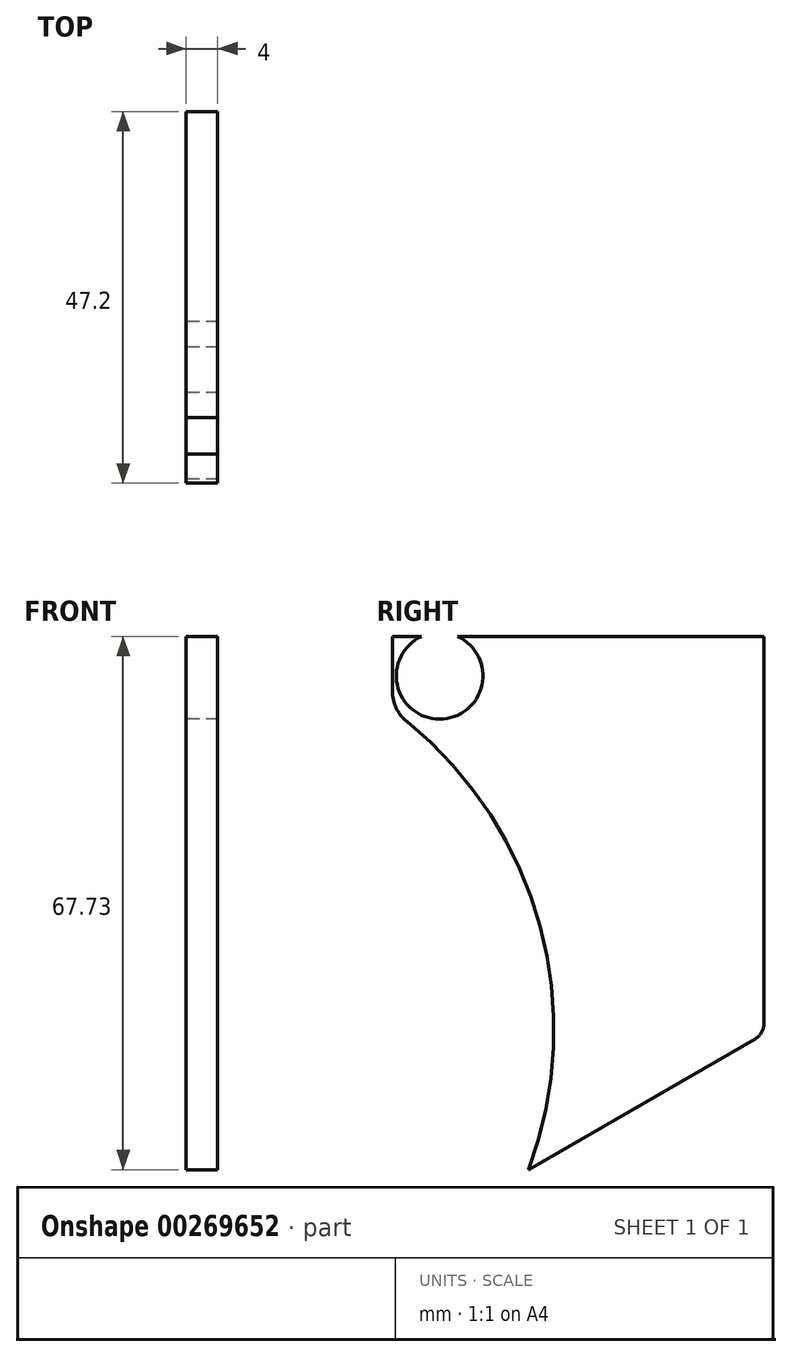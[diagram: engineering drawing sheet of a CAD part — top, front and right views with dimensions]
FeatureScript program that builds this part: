
annotation { "Feature Type Name" : "Feature", "Feature Type Description" : "" }
export const myFeature = defineFeature(function(context is Context, id is Id, definition is map)
    precondition{}
    {
        {
            var Q0;
            Q0=qCreatedBy(makeId("Right.planeOp"),FACE);
            var sketch = newSketch(context, id + "F0", { "sketchPlane" : qUnion([Q0])});
            skLineSegment(sketch, "E0", {"start": v(50, -52.08) * mm, "end": v(50, 0) * mm});
            skLineSegment(sketch, "E1", {"start": v(50, 0) * mm, "end": v(0, 0) * mm});
            skArc(sketch, "E2", {"start": v(-77.52, -32.91) * mm, "mid": v(-15.33, -98.32) * mm, "end": v(0, -9.38) * mm});
            skLineSegment(sketch, "E3", {"start": v(0, 0) * mm, "end": v(0, -9.38) * mm});
            skLineSegment(sketch, "E4", {"start": v(50, -52.08) * mm, "end": v(28.18, -64.68) * mm});
            skCircle(sketch, "E5", {"center": v(-30, -50) * mm, "radius": 50.5 * mm, "construction": true});
            skLineSegment(sketch, "E6", {"start": v(-77.52, -32.91) * mm, "end": v(-87.52, -32.91) * mm});
            skLineSegment(sketch, "E7", {"start": v(-15, -140.5) * mm, "end": v(-15, -108.1) * mm});
            skLineSegment(sketch, "E8", {"start": v(-45, -108.1) * mm, "end": v(-45, -140.5) * mm});
            skLineSegment(sketch, "E9", {"start": v(-45, -140.5) * mm, "end": v(-15, -140.5) * mm});
            skArc(sketch, "E10", {"start": v(-15, -108.1) * mm, "mid": v(12.54, -92.3) * mm, "end": v(28.18, -64.68) * mm});
            skArc(sketch, "E11.trimOffspring", {"start": v(-87.52, -32.91) * mm, "mid": v(-82.23, -79.54) * mm, "end": v(-45, -108.1) * mm});
            skLineSegment(sketch, "E12", {"start": v(-30, -50) * mm, "end": v(-30, -129.79) * mm, "construction": true});
            skSolve(sketch);
        }
        {
            var Q0;
            Q0=qSketchRegion(id+"F0",true);
            extrude(context, id + "F1", {"entities" : qUnion([Q0]), "depth" : 34 * mm});
        }
        {
            var Q0;
            Q0=makeQuery(id+"F1.opExtrude","SWEPT_EDGE",EDGE,{"disambiguationData":[OSD([sQuery(id+"F0.wireOp",EDGE,"E0"),sQuery(id+"F0.wireOp",EDGE,"E4")])]});
            var Q1;
            Q1=makeQuery(id+"F1.opExtrude","SWEPT_EDGE",EDGE,{"disambiguationData":[OSD([sQuery(id+"F0.wireOp",EDGE,"E2"),sQuery(id+"F0.wireOp",EDGE,"E3")])]});
            fillet(context, id + "F2", {"entities" : qUnion([Q0, Q1]), "radius" : 5 * mm, "tangentPropagation" : true, "allowEdgeOverflow" : false});
        }
        {
            var Q0;
            Q0=makeQuery(id+"F1.opExtrude","SWEPT_FACE",FACE,{"disambiguationData":[OSD([sQuery(id+"F0.wireOp",EDGE,"E1")])]});
            var Q1;
            Q1=makeQuery(id+"F1.opExtrude","SWEPT_FACE",FACE,{"disambiguationData":[OSD([sQuery(id+"F0.wireOp",EDGE,"E2")])]});
            var Q2;
            Q2=makeQuery(id+"F2.opFillet","BLEND_FACE",FACE,{"disambiguationData":[OSD([sQuery(id+"F0.wireOp",EDGE,"E2"),sQuery(id+"F0.wireOp",EDGE,"E3")])]});
            var Q3;
            Q3=makeQuery(id+"F1.opExtrude","SWEPT_FACE",FACE,{"disambiguationData":[OSD([sQuery(id+"F0.wireOp",EDGE,"E3")])]});
            var Q4;
            Q4=makeQuery(id+"F1.opExtrude","SWEPT_FACE",FACE,{"disambiguationData":[OSD([sQuery(id+"F0.wireOp",EDGE,"E6")])]});
            var Q5;
            Q5=makeQuery(id+"F1.opExtrude","SWEPT_FACE",FACE,{"disambiguationData":[OSD([sQuery(id+"F0.wireOp",EDGE,"E9")])]});
            shell(context, id + "F3", {"entities" : qUnion([Q0, Q1, Q2, Q3, Q4, Q5]), "thickness" : 2.4 * mm});
        }
        {
            var Q0;
            Q0=makeQuery(id+"F1.opExtrude","CAP_FACE",FACE,{"disambiguationData":[OSD([sQuery(id+"F0.wireOp",EDGE,"E0"),sQuery(id+"F0.wireOp",EDGE,"E1"),sQuery(id+"F0.wireOp",EDGE,"E2"),sQuery(id+"F0.wireOp",EDGE,"E3"),sQuery(id+"F0.wireOp",EDGE,"E4"),sQuery(id+"F0.wireOp",EDGE,"E6"),sQuery(id+"F0.wireOp",EDGE,"E7"),sQuery(id+"F0.wireOp",EDGE,"E8"),sQuery(id+"F0.wireOp",EDGE,"E9"),sQuery(id+"F0.wireOp",EDGE,"E10"),sQuery(id+"F0.wireOp",EDGE,"E11.trimOffspring")])],"isStart":false});
            var sketch = newSketch(context, id + "F4", { "sketchPlane" : qUnion([Q0])});
            skArc(sketch, "E13.0", {"start": v(-17.9, -99.03) * mm, "mid": v(3.32, -87.94) * mm, "end": v(17.06, -68.32) * mm, "construction": true});
            skArc(sketch, "E14", {"start": v(-17.9, -108.77) * mm, "mid": v(12.64, -92.2) * mm, "end": v(28.89, -61.5) * mm});
            skPoint(sketch, "E15.orphan", {"position": v(1.85, -10.8) * mm});
            skArc(sketch, "E16", {"start": v(-77.52, -32.91) * mm, "mid": v(-47.7, -97.3) * mm, "end": v(17.06, -68.32) * mm});
            skLineSegment(sketch, "E17.0", {"start": v(28.89, -61.5) * mm, "end": v(17.06, -68.32) * mm});
            skPoint(sketch, "E18.orphan", {"position": v(26.09, -63.11) * mm});
            skPoint(sketch, "E19.orphan", {"position": v(-17.4, -106.2) * mm});
            skPoint(sketch, "E20.orphan", {"position": v(46.3, -51.44) * mm});
            skPoint(sketch, "E21.orphan", {"position": v(28.18, -64.68) * mm});
            skPoint(sketch, "E22.orphan", {"position": v(-15, -108.1) * mm});
            skLineSegment(sketch, "E23", {"start": v(-17.9, -99.03) * mm, "end": v(-17.9, -108.77) * mm});
            skSolve(sketch);
        }
        {
            var Q0;
            Q0=qSketchRegion(id+"F4",true);
            var Q1;
            {var subQ0=sQuery(id+"F0.wireOp",EDGE,"E11.trimOffspring");var subQ1=sQuery(id+"F0.wireOp",EDGE,"E10");var subQ2=sQuery(id+"F0.wireOp",EDGE,"E9");var subQ3=sQuery(id+"F0.wireOp",EDGE,"E8");var subQ4=sQuery(id+"F0.wireOp",EDGE,"E7");var subQ5=sQuery(id+"F0.wireOp",EDGE,"E6");var subQ6=sQuery(id+"F0.wireOp",EDGE,"E4");var subQ7=sQuery(id+"F0.wireOp",EDGE,"E3");var subQ8=sQuery(id+"F0.wireOp",EDGE,"E2");var subQ9=sQuery(id+"F0.wireOp",EDGE,"E1");var subQ10=sQuery(id+"F0.wireOp",EDGE,"E0");Q1=makeQuery(id+"F3.opShell","OFFSET_FACE",FACE,{"disambiguationData":[OSD([subQ10,subQ9,subQ8,subQ7,subQ6,subQ5,subQ4,subQ3,subQ2,subQ1,subQ0]),TDD([makeQuery(id+"F1.opExtrude","CAP_FACE",FACE,{"disambiguationData":[OSD([subQ10,subQ9,subQ8,subQ7,subQ6,subQ5,subQ4,subQ3,subQ2,subQ1,subQ0])],"isStart":true})])]});}
            extrude(context, id + "F5", {"entities" : qUnion([Q0]), "operationType" : NewBodyOperationType.ADD, "endBound" : BoundingType.UP_TO_SURFACE, "oppositeDirection" : true, "endBoundEntityFace" : qUnion([Q1]), "depth" : 25 * mm});
        }
        {
            var Q0;
            Q0=makeQuery(id+"F1.opExtrude","CAP_FACE",FACE,{"disambiguationData":[OSD([sQuery(id+"F0.wireOp",EDGE,"E0"),sQuery(id+"F0.wireOp",EDGE,"E1"),sQuery(id+"F0.wireOp",EDGE,"E2"),sQuery(id+"F0.wireOp",EDGE,"E3"),sQuery(id+"F0.wireOp",EDGE,"E4")])],"isStart":true});
            var sketch = newSketch(context, id + "F6", { "sketchPlane" : qUnion([Q0])});
            skCircle(sketch, "E24", {"center": v(-6, -5) * mm, "radius": 2.5 * mm});
            skCircle(sketch, "E25", {"center": v(-15.77, -82.6) * mm, "radius": 2.5 * mm});
            skArc(sketch, "E26.0", {"start": v(77.52, -32.91) * mm, "mid": v(16.45, -98.65) * mm, "end": v(-1.85, -10.8) * mm, "construction": true});
            skLineSegment(sketch, "E27", {"start": v(30, -50) * mm, "end": v(-6, -5) * mm, "construction": true});
            skLineSegment(sketch, "E28", {"start": v(30, -50) * mm, "end": v(-15.77, -82.6) * mm, "construction": true});
            skLineSegment(sketch, "E29", {"start": v(-6, -5) * mm, "end": v(-15.77, -82.6) * mm, "construction": true});
            skSolve(sketch);
        }
        {
            var Q0;
            Q0=qSketchRegion(id+"F6",true);
            var Q1;
            Q1=makeQuery(id+"F1.opExtrude","CAP_FACE",FACE,{"disambiguationData":[OSD([sQuery(id+"F0.wireOp",EDGE,"E0"),sQuery(id+"F0.wireOp",EDGE,"E1"),sQuery(id+"F0.wireOp",EDGE,"E2"),sQuery(id+"F0.wireOp",EDGE,"E3"),sQuery(id+"F0.wireOp",EDGE,"E4"),sQuery(id+"F0.wireOp",EDGE,"E6"),sQuery(id+"F0.wireOp",EDGE,"E7"),sQuery(id+"F0.wireOp",EDGE,"E8"),sQuery(id+"F0.wireOp",EDGE,"E9"),sQuery(id+"F0.wireOp",EDGE,"E10"),sQuery(id+"F0.wireOp",EDGE,"E11.trimOffspring")])],"isStart":true});
            extrude(context, id + "F7", {"entities" : qUnion([Q0]), "operationType" : NewBodyOperationType.REMOVE, "endBound" : BoundingType.THROUGH_ALL, "oppositeDirection" : true, "endBoundEntityFace" : qUnion([Q1]), "depth" : 25 * mm});
        }
        {
            var Q0;
            Q0=makeQuery(id+"F5.opExtrude","SWEPT_EDGE",EDGE,{"disambiguationData":[OSD([sQuery(id+"F4.wireOp",EDGE,"E16"),sQuery(id+"F4.wireOp",EDGE,"E23")])]});
            fillet(context, id + "F8", {"entities" : qUnion([Q0]), "radius" : 5 * mm, "tangentPropagation" : true, "allowEdgeOverflow" : false});
        }
        {
            var Q0;
            Q0=makeQuery(id+"F1.opExtrude","SWEPT_FACE",FACE,{"disambiguationData":[OSD([sQuery(id+"F0.wireOp",EDGE,"E10")])]});
            shell(context, id + "F9", {"entities" : qUnion([Q0]), "thickness" : 2.4 * mm});
        }
        {
            var Q0;
            {var subQ0=sQuery(id+"F0.wireOp",EDGE,"E4");var subQ1=sQuery(id+"F0.wireOp",EDGE,"E0");var subQ2=sQuery(id+"F0.wireOp",EDGE,"E3");var subQ3=sQuery(id+"F0.wireOp",EDGE,"E2");var subQ4=sQuery(id+"F0.wireOp",EDGE,"E1");var subQ5=sQuery(id+"F0.wireOp",EDGE,"E11.trimOffspring");var subQ6=sQuery(id+"F0.wireOp",EDGE,"E10");var subQ7=sQuery(id+"F0.wireOp",EDGE,"E9");var subQ8=sQuery(id+"F0.wireOp",EDGE,"E8");var subQ9=sQuery(id+"F0.wireOp",EDGE,"E7");var subQ10=sQuery(id+"F0.wireOp",EDGE,"E6");Q0=makeQuery(id+"F5.boolean.opBoolean","SPLIT",FACE,{"disambiguationData":[TD([makeQuery(id+"F1.opExtrude","SWEPT_FACE",FACE,{"disambiguationData":[OSD([subQ4])]})])],"derivedFrom":makeQuery(id+"F3.opShell","OFFSET_FACE",FACE,{"disambiguationData":[OSD([subQ1,subQ4,subQ3,subQ2,subQ0,subQ10,subQ9,subQ8,subQ7,subQ6,subQ5]),TDD([makeQuery(id+"F1.opExtrude","CAP_FACE",FACE,{"disambiguationData":[OSD([subQ1,subQ4,subQ3,subQ2,subQ0,subQ10,subQ9,subQ8,subQ7,subQ6,subQ5])],"isStart":true})])]})});}
            cPlane(context, id + "F10", {"entities" : qUnion([Q0]), "cplaneType" : CPlaneType.OFFSET, "offset" : 7 * mm, "width" : 150 * mm, "height" : 150 * mm});
        }
        {
            var Q0;
            Q0=qCreatedBy(id+"F10.planeOp",FACE);
            var sketch = newSketch(context, id + "F11", { "sketchPlane" : qUnion([Q0])});
            skLineSegment(sketch, "E30.0", {"start": v(47.6, 0) * mm, "end": v(0, 0) * mm});
            skLineSegment(sketch, "E31.0", {"start": v(47.6, -49.19) * mm, "end": v(47.6, 0) * mm});
            skArc(sketch, "E32.0", {"start": v(47.6, -49.19) * mm, "mid": v(47.25, -50.49) * mm, "end": v(46.3, -51.44) * mm});
            skLineSegment(sketch, "E33.0", {"start": v(46.3, -51.44) * mm, "end": v(17.06, -68.32) * mm});
            skArc(sketch, "E34.0", {"start": v(17.06, -68.32) * mm, "mid": v(18.82, -37.09) * mm, "end": v(1.85, -10.8) * mm});
            skArc(sketch, "E35.0", {"start": v(1.85, -10.8) * mm, "mid": v(0.49, -9.08) * mm, "end": v(0, -6.93) * mm});
            skLineSegment(sketch, "E36.0", {"start": v(0, 0) * mm, "end": v(0, -6.93) * mm});
            skCircle(sketch, "E37.0", {"center": v(6, -5) * mm, "radius": 2.5 * mm});
            skSolve(sketch);
        }
        {
            var Q0;
            Q0=qSketchRegion(id+"F11",true);
            extrude(context, id + "F12", {"entities" : qUnion([Q0]), "operationType" : NewBodyOperationType.ADD, "depth" : 4 * mm});
        }
        {
            var Q0;
            Q0=makeQuery(id+"F6.imprint","IMPRINT",FACE,{"disambiguationData":[TD([[makeQuery(id+"F6.imprint","IMPRINT",EDGE,{"derivedFrom":sQuery(id+"F6.wireOp",EDGE,"E24")}),-1.0]])]});
            var sketch = newSketch(context, id + "F13", { "sketchPlane" : qUnion([Q0])});
            skCircle(sketch, "E38.0", {"center": v(-6, -5) * mm, "radius": 2.5 * mm});
            skCircle(sketch, "E39", {"center": v(-6, -5) * mm, "radius": 5 * mm});
            skSolve(sketch);
        }
        {
            var Q0;
            Q0=qSketchRegion(id+"F13",true);
            var Q1;
            {var subQ0=sQuery(id+"F0.wireOp",EDGE,"E4");var subQ1=sQuery(id+"F0.wireOp",EDGE,"E0");var subQ2=sQuery(id+"F0.wireOp",EDGE,"E3");var subQ3=sQuery(id+"F0.wireOp",EDGE,"E2");var subQ4=sQuery(id+"F0.wireOp",EDGE,"E1");var subQ5=sQuery(id+"F0.wireOp",EDGE,"E11.trimOffspring");var subQ6=sQuery(id+"F0.wireOp",EDGE,"E10");var subQ7=sQuery(id+"F0.wireOp",EDGE,"E9");var subQ8=sQuery(id+"F0.wireOp",EDGE,"E8");var subQ9=sQuery(id+"F0.wireOp",EDGE,"E7");var subQ10=sQuery(id+"F0.wireOp",EDGE,"E6");Q1=makeQuery(id+"F5.boolean.opBoolean","SPLIT",FACE,{"disambiguationData":[TD([makeQuery(id+"F1.opExtrude","SWEPT_FACE",FACE,{"disambiguationData":[OSD([subQ4])]})])],"derivedFrom":makeQuery(id+"F3.opShell","OFFSET_FACE",FACE,{"disambiguationData":[OSD([subQ1,subQ4,subQ3,subQ2,subQ0,subQ10,subQ9,subQ8,subQ7,subQ6,subQ5]),TDD([makeQuery(id+"F1.opExtrude","CAP_FACE",FACE,{"disambiguationData":[OSD([subQ1,subQ4,subQ3,subQ2,subQ0,subQ10,subQ9,subQ8,subQ7,subQ6,subQ5])],"isStart":false})])]})});}
            extrude(context, id + "F14", {"entities" : qUnion([Q0]), "operationType" : NewBodyOperationType.ADD, "endBound" : BoundingType.UP_TO_SURFACE, "oppositeDirection" : true, "endBoundEntityFace" : qUnion([Q1]), "depth" : 25 * mm});
        }
        {
            var Q0;
            Q0=makeQuery(id+"F6.imprint","IMPRINT",FACE,{"disambiguationData":[TD([[makeQuery(id+"F6.imprint","IMPRINT",EDGE,{"derivedFrom":sQuery(id+"F6.wireOp",EDGE,"E24")}),-1.0]])]});
            var sketch = newSketch(context, id + "F15", { "sketchPlane" : qUnion([Q0])});
            skLineSegment(sketch, "E40.0", {"start": v(45, -109.49) * mm, "end": v(45, -114.49) * mm});
            skLineSegment(sketch, "E41.0", {"start": v(15, -114.49) * mm, "end": v(15, -109.49) * mm});
            skLineSegment(sketch, "E42.bottom", {"start": v(5, -109.49) * mm, "end": v(15, -109.49) * mm});
            skLineSegment(sketch, "E42.top", {"start": v(5, -114.49) * mm, "end": v(15, -114.49) * mm});
            skLineSegment(sketch, "E42.left", {"start": v(5, -109.49) * mm, "end": v(5, -114.49) * mm});
            skLineSegment(sketch, "E42.right", {"start": v(55, -109.49) * mm, "end": v(55, -114.49) * mm});
            skLineSegment(sketch, "E43.trimOffspring", {"start": v(45, -109.49) * mm, "end": v(55, -109.49) * mm});
            skLineSegment(sketch, "E44.trimOffspring", {"start": v(45, -114.49) * mm, "end": v(55, -114.49) * mm});
            skPoint(sketch, "E45.orphan", {"position": v(15, -140.5) * mm});
            skPoint(sketch, "E46.orphan", {"position": v(45, -140.5) * mm});
            skPoint(sketch, "E47.orphan", {"position": v(45, -108.1) * mm});
            skPoint(sketch, "E48.orphan", {"position": v(15, -108.1) * mm});
            skSolve(sketch);
        }
        {
            var Q0;
            Q0=qSketchRegion(id+"F15",true);
            var Q1;
            Q1=makeQuery(id+"F1.opExtrude","CAP_FACE",FACE,{"disambiguationData":[OSD([sQuery(id+"F0.wireOp",EDGE,"E0"),sQuery(id+"F0.wireOp",EDGE,"E1"),sQuery(id+"F0.wireOp",EDGE,"E2"),sQuery(id+"F0.wireOp",EDGE,"E3"),sQuery(id+"F0.wireOp",EDGE,"E4"),sQuery(id+"F0.wireOp",EDGE,"E6"),sQuery(id+"F0.wireOp",EDGE,"E7"),sQuery(id+"F0.wireOp",EDGE,"E8"),sQuery(id+"F0.wireOp",EDGE,"E9"),sQuery(id+"F0.wireOp",EDGE,"E10"),sQuery(id+"F0.wireOp",EDGE,"E11.trimOffspring")])],"isStart":false});
            extrude(context, id + "F16", {"entities" : qUnion([Q0]), "operationType" : NewBodyOperationType.ADD, "endBound" : BoundingType.UP_TO_SURFACE, "oppositeDirection" : true, "endBoundEntityFace" : qUnion([Q1]), "depth" : 25 * mm});
        }
        {
            var Q0;
            {var subQ2=sQuery(id+"F0.wireOp",EDGE,"E9");var subQ5=sQuery(id+"F0.wireOp",EDGE,"E8");Q0=makeQuery(id+"F16.boolean.opBoolean","SPLIT",FACE,{"disambiguationData":[TD([makeQuery(id+"F1.opExtrude","SWEPT_FACE",FACE,{"disambiguationData":[OSD([subQ2])]})])],"derivedFrom":makeQuery(id+"F1.opExtrude","SWEPT_FACE",FACE,{"disambiguationData":[OSD([subQ5])]})});}
            var sketch = newSketch(context, id + "F17", { "sketchPlane" : qUnion([Q0])});
            skLineSegment(sketch, "E49", {"start": v(0, -127.5) * mm, "end": v(34, -127.5) * mm, "construction": true});
            skLineSegment(sketch, "E50", {"start": v(17, -140.5) * mm, "end": v(17, -114.49) * mm, "construction": true});
            skCircle(sketch, "E51", {"center": v(17, -127.5) * mm, "radius": 2.1 * mm});
            skSolve(sketch);
        }
        {
            var Q0;
            Q0=qSketchRegion(id+"F17",true);
            extrude(context, id + "F18", {"entities" : qUnion([Q0]), "operationType" : NewBodyOperationType.REMOVE, "endBound" : BoundingType.THROUGH_ALL, "oppositeDirection" : true, "depth" : 25 * mm});
        }
        {
            var Q0;
            Q0=makeQuery(id+"F12.opExtrude","CAP_FACE",FACE,{"disambiguationData":[OSD([sQuery(id+"F11.wireOp",EDGE,"E30.0"),sQuery(id+"F11.wireOp",EDGE,"E31.0"),sQuery(id+"F11.wireOp",EDGE,"E32.0"),sQuery(id+"F11.wireOp",EDGE,"E33.0"),sQuery(id+"F11.wireOp",EDGE,"E34.0"),sQuery(id+"F11.wireOp",EDGE,"E35.0"),sQuery(id+"F11.wireOp",EDGE,"E36.0"),sQuery(id+"F11.wireOp",EDGE,"E37.0")])],"isStart":true});
            var sketch = newSketch(context, id + "F19", { "sketchPlane" : qUnion([Q0])});
            skLineSegment(sketch, "E52.bottom", {"start": v(-63.7, 10.52) * mm, "end": v(126.2, 10.52) * mm});
            skLineSegment(sketch, "E52.top", {"start": v(-63.7, -153.85) * mm, "end": v(126.2, -153.85) * mm});
            skLineSegment(sketch, "E52.left", {"start": v(-63.7, 10.52) * mm, "end": v(-63.7, -153.85) * mm});
            skLineSegment(sketch, "E52.right", {"start": v(126.2, 10.52) * mm, "end": v(126.2, -153.85) * mm});
            skSolve(sketch);
        }
        {
            var Q0;
            {var subQ3=sQuery(id+"F11.wireOp",EDGE,"E34.0");Q0=makeQuery(id+"F19.imprint","IMPRINT",FACE,{"disambiguationData":[TD([[makeQuery(id+"F19.imprint","IMPRINT",EDGE,{"derivedFrom":makeQuery(id+"F12.opExtrude","CAP_EDGE",EDGE,{"disambiguationData":[OSD([subQ3])],"isStart":true})}),1.0]])]});}
            var sketch = newSketch(context, id + "F20", { "sketchPlane" : qUnion([Q0])});
            skCircle(sketch, "E53.0", {"center": v(-6, -5) * mm, "radius": 5.5 * mm});
            skSolve(sketch);
        }
        {
            var Q0;
            Q0 = qSketchRegion(id + "F19", true);
            extrude(context, id + "F21", {"entities" : qUnion([Q0]), "operationType" : NewBodyOperationType.REMOVE, "endBound" : BoundingType.THROUGH_ALL, "depth" : 25 * mm});
        }
        {
            var Q0;
            Q0=makeQuery(id+"F21.boolean.opBoolean","MERGE",FACE,{"derivedFrom":[makeQuery(id+"F12.opExtrude","CAP_FACE",FACE,{"disambiguationData":[OSD([sQuery(id+"F11.wireOp",EDGE,"E30.0"),sQuery(id+"F11.wireOp",EDGE,"E31.0"),sQuery(id+"F11.wireOp",EDGE,"E32.0"),sQuery(id+"F11.wireOp",EDGE,"E33.0"),sQuery(id+"F11.wireOp",EDGE,"E34.0"),sQuery(id+"F11.wireOp",EDGE,"E35.0"),sQuery(id+"F11.wireOp",EDGE,"E36.0"),sQuery(id+"F11.wireOp",EDGE,"E37.0")])],"isStart":true}),makeQuery(id+"F21.opExtrude","CAP_FACE",FACE,{"disambiguationData":[OSD([sQuery(id+"F19.wireOp",EDGE,"E52.bottom"),sQuery(id+"F19.wireOp",EDGE,"E52.top"),sQuery(id+"F19.wireOp",EDGE,"E52.left"),sQuery(id+"F19.wireOp",EDGE,"E52.right")])],"isStart":true})]});
            var sketch = newSketch(context, id + "F22", { "sketchPlane" : qUnion([Q0])});
            skLineSegment(sketch, "E54.0", {"start": v(-46.3, -51.44) * mm, "end": v(-17.06, -68.32) * mm});
            skLineSegment(sketch, "E55", {"start": v(-17.06, -68.32) * mm, "end": v(97.63, -13.25) * mm});
            skLineSegment(sketch, "E56", {"start": v(97.63, -13.25) * mm, "end": v(124.38, -131.2) * mm});
            skLineSegment(sketch, "E57", {"start": v(124.38, -131.2) * mm, "end": v(20.78, -157.05) * mm});
            skLineSegment(sketch, "E58", {"start": v(20.78, -157.05) * mm, "end": v(-89.3, -69.99) * mm});
            skLineSegment(sketch, "E59.0", {"start": v(-47.6, -49.19) * mm, "end": v(-47.6, 0) * mm});
            skArc(sketch, "E60", {"start": v(-47.6, -49.19) * mm, "mid": v(-47.25, -50.49) * mm, "end": v(-46.3, -51.44) * mm});
            skLineSegment(sketch, "E61", {"start": v(-64.25, 0) * mm, "end": v(-47.6, 0) * mm});
            skLineSegment(sketch, "E62", {"start": v(-64.25, 0) * mm, "end": v(-89.3, -69.99) * mm});
            skSolve(sketch);
        }
        {
            var Q0;
            Q0 = qSketchRegion(id + "F22", true);
            extrude(context, id + "F23", {"entities" : qUnion([Q0]), "operationType" : NewBodyOperationType.REMOVE, "oppositeDirection" : true, "depth" : 25 * mm});
        }
        {
            var Q0;
            Q0=makeQuery(id+"F12.opExtrude","CAP_FACE",FACE,{"disambiguationData":[OSD([sQuery(id+"F11.wireOp",EDGE,"E30.0"),sQuery(id+"F11.wireOp",EDGE,"E31.0"),sQuery(id+"F11.wireOp",EDGE,"E32.0"),sQuery(id+"F11.wireOp",EDGE,"E33.0"),sQuery(id+"F11.wireOp",EDGE,"E34.0"),sQuery(id+"F11.wireOp",EDGE,"E35.0"),sQuery(id+"F11.wireOp",EDGE,"E36.0"),sQuery(id+"F11.wireOp",EDGE,"E37.0")])],"isStart":false});
            var sketch = newSketch(context, id + "F24", { "sketchPlane" : qUnion([Q0])});
            skLineSegment(sketch, "E63.bottom", {"start": v(-62.95, 12.76) * mm, "end": v(97.94, 12.76) * mm});
            skLineSegment(sketch, "E63.top", {"start": v(-62.95, -97.2) * mm, "end": v(97.94, -97.2) * mm});
            skLineSegment(sketch, "E63.left", {"start": v(-62.95, 12.76) * mm, "end": v(-62.95, -97.2) * mm});
            skLineSegment(sketch, "E63.right", {"start": v(97.94, 12.76) * mm, "end": v(97.94, -97.2) * mm});
            skSolve(sketch);
        }
        {
            var Q0;
            Q0 = qSketchRegion(id + "F24", true);
            extrude(context, id + "F25", {"entities" : qUnion([Q0]), "operationType" : NewBodyOperationType.REMOVE, "endBound" : BoundingType.THROUGH_ALL, "depth" : 25 * mm});
        }
        {
            var Q0;
            Q0 = qSketchRegion(id + "F20", true);
            var Q1;
            Q1 = qConstructionFilter(qBodyType(qCreatedBy(id + "F20" ,EDGE), BodyType.WIRE), ConstructionObject.NO);
            extrude(context, id + "F26", {"entities" : qUnion([Q0]), "operationType" : NewBodyOperationType.REMOVE, "surfaceEntities" : qUnion([Q1]), "endBound" : BoundingType.THROUGH_ALL, "oppositeDirection" : true, "depth" : 25 * mm});
        }
        {
            var Q0;
            Q0=makeQuery(id+"F21.boolean.opBoolean","MERGE",FACE,{"derivedFrom":[makeQuery(id+"F12.opExtrude","CAP_FACE",FACE,{"disambiguationData":[OSD([sQuery(id+"F11.wireOp",EDGE,"E30.0"),sQuery(id+"F11.wireOp",EDGE,"E31.0"),sQuery(id+"F11.wireOp",EDGE,"E32.0"),sQuery(id+"F11.wireOp",EDGE,"E33.0"),sQuery(id+"F11.wireOp",EDGE,"E34.0"),sQuery(id+"F11.wireOp",EDGE,"E35.0"),sQuery(id+"F11.wireOp",EDGE,"E36.0"),sQuery(id+"F11.wireOp",EDGE,"E37.0")])],"isStart":true}),makeQuery(id+"F21.opExtrude","CAP_FACE",FACE,{"disambiguationData":[OSD([sQuery(id+"F19.wireOp",EDGE,"E52.bottom"),sQuery(id+"F19.wireOp",EDGE,"E52.top"),sQuery(id+"F19.wireOp",EDGE,"E52.left"),sQuery(id+"F19.wireOp",EDGE,"E52.right")])],"isStart":true})]});
            var sketch = newSketch(context, id + "F27", { "sketchPlane" : qUnion([Q0])});
            skLineSegment(sketch, "E64.0", {"start": v(-47.2, -49.19) * mm, "end": v(-47.2, 2.75) * mm});
            skLineSegment(sketch, "E64.1", {"start": v(-46.1, -51.1) * mm, "end": v(-14.82, -69.15) * mm});
            skArc(sketch, "E65.0", {"start": v(-47.2, -49.19) * mm, "mid": v(-46.9, -50.29) * mm, "end": v(-46.1, -51.1) * mm});
            skLineSegment(sketch, "E66", {"start": v(-47.2, 2.75) * mm, "end": v(-59.6, 2.75) * mm});
            skLineSegment(sketch, "E67", {"start": v(-59.6, 2.75) * mm, "end": v(-59.6, -69.74) * mm});
            skLineSegment(sketch, "E68", {"start": v(-59.6, -69.74) * mm, "end": v(-14.82, -70.3) * mm});
            skLineSegment(sketch, "E69", {"start": v(-14.82, -70.3) * mm, "end": v(-14.82, -69.15) * mm});
            skSolve(sketch);
        }
        {
            var Q0;
            Q0 = qSketchRegion(id + "F27", true);
            extrude(context, id + "F28", {"entities" : qUnion([Q0]), "operationType" : NewBodyOperationType.REMOVE, "endBound" : BoundingType.THROUGH_ALL, "oppositeDirection" : true, "depth" : 25 * mm});
        }
    });
